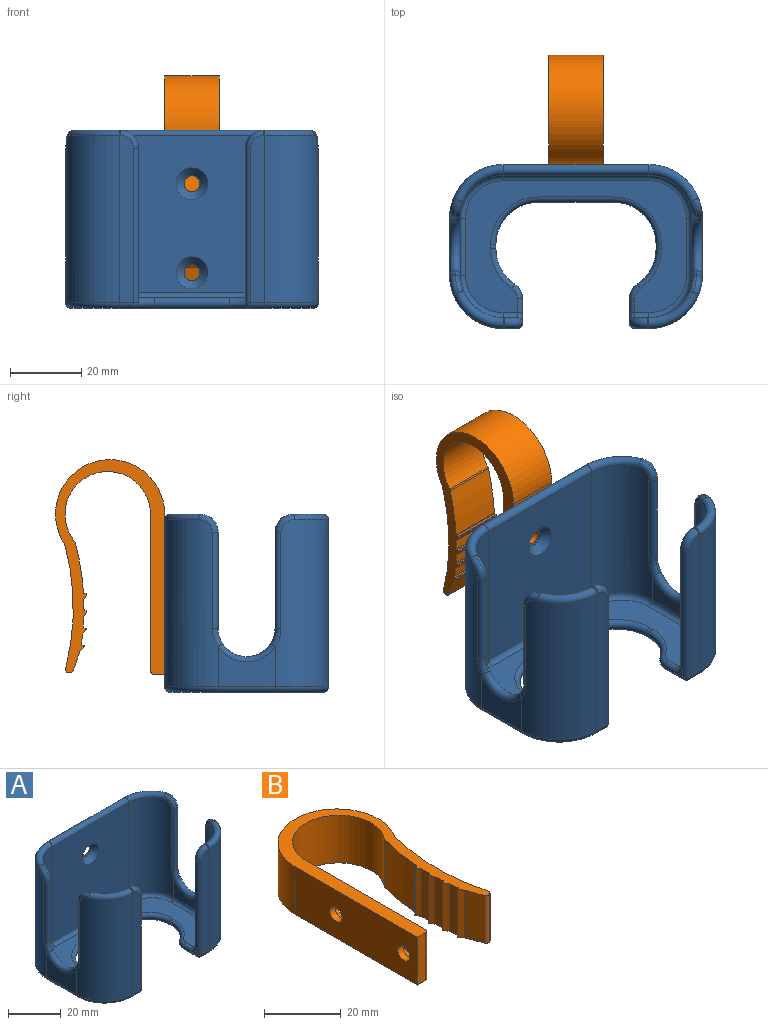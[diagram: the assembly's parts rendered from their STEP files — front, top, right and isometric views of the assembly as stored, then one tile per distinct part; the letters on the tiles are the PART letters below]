
ASSEMBLY  parts=2 mates=1
PART A: 92 faces, bbox 73.5x48.5x50.4 mm
  f0: plane 47x4mm, normal (0,-1,0), area 185.4mm2, adj f16,f69,f73,f77,f78
  f1: plane 62x37mm, normal (0,0,1), area 856.6mm2, adj f48,f52,f53,f57,f59,f62,f63,f67
  f2: plane 44x4mm, normal (0,1,0), area 173.4mm2, adj f12,f69,f73,f77,f80
  f3: plane 16x11.38mm, normal (1,0,0), area 132.7mm2, adj f16,f17,f44,f70
  f4: plane 68x43mm, normal (0,0,-1), area 1325.8mm2, adj f45,f46,f50,f56,f57,f61,f62,f66
  f5: plane 47x4mm, normal (0,-1,0), area 185.4mm2, adj f19,f40,f42,f46,f47
  f6: plane 47x41mm, normal (0,1,0), area 1895.2mm2, adj f17,f18,f30,f61,f88,f90
  f7: plane 16x8.38mm, normal (-1,0,0), area 84.7mm2, adj f12,f15,f44,f72
  f8: plane 44x4mm, normal (0,1,0), area 173.4mm2, adj f13,f40,f42,f47,f52
  f9: plane 16x8.38mm, normal (1,0,0), area 84.7mm2, adj f13,f14,f25,f53
  f10: plane 44x41mm, normal (0,-1,0), area 1677.9mm2, adj f14,f15,f30,f63,f89,f91
  f11: plane 16x11.38mm, normal (-1,0,0), area 132.7mm2, adj f18,f19,f25,f50
  f12: cylinder r=12mm len=44mm, axis (0,0,-1), area 781.6mm2, adj f2,f7,f54,f55,f64,f65,f76
  f13: cylinder r=12mm len=44mm, axis (0,0,1), area 781.6mm2, adj f8,f9,f31,f32,f36,f37,f48
  f14: cylinder r=12mm len=44mm, axis (0,0,-1), area 781.6mm2, adj f9,f10,f22,f26,f27,f28,f59
  f15: cylinder r=12mm len=44mm, axis (0,0,1), area 781.6mm2, adj f7,f10,f33,f38,f39,f43,f68
  f16: cylinder r=15mm len=47mm, axis (0,0,1), area 1047.7mm2, adj f0,f3,f49,f55,f60,f65,f74
  f17: cylinder r=15mm len=47mm, axis (0,0,-1), area 1047.7mm2, adj f3,f6,f33,f35,f39,f41,f66
  f18: cylinder r=15mm len=47mm, axis (0,0,1), area 1047.7mm2, adj f6,f11,f22,f23,f24,f28,f56
  f19: cylinder r=15mm len=47mm, axis (0,0,-1), area 1047.7mm2, adj f5,f11,f29,f31,f34,f36,f45
  f20: plane 3x3mm, normal (1,0,0), area 1.9mm2, adj f47,f57,f58
  f21: plane 3x3mm, normal (-1,0,0), area 1.9mm2, adj f77,f83,f84
  f22: cylinder r=1.5mm len=27mm, axis (0,0,1), area 127.2mm2, adj f14,f18,f23,f24,f26,f27
  f23: bspline ~7x3.44mm, area 12.1mm2, adj f18,f22,f25,f26
  f24: bspline ~6.77x5.33mm, area 18.5mm2, adj f18,f22,f27,f28
  f25: torus R=9.5mm, axis (-1,0,0), area 80.6mm2, adj f9,f11,f23,f26,f29,f32
  f26: bspline ~7x3.08mm, area 10.9mm2, adj f14,f22,f23,f25
  f27: bspline ~6.21x5.34mm, area 15mm2, adj f14,f22,f24,f28
  f28: torus R=13.5mm, axis (0,0,1), area 75.8mm2, adj f14,f18,f24,f27,f30
  f29: bspline ~6x3.18mm, area 12.1mm2, adj f19,f25,f31,f32
  f30: cylinder r=1.5mm len=41mm, axis (1,0,0), area 193.2mm2, adj f6,f10,f28,f33
  f31: cylinder r=1.5mm len=27mm, axis (0,0,-1), area 127.2mm2, adj f13,f19,f29,f32,f34,f37
  f32: bspline ~7.15x3.65mm, area 10.9mm2, adj f13,f25,f29,f31
  f33: torus R=13.5mm, axis (0,0,1), area 75.8mm2, adj f15,f17,f30,f35,f38
  f34: bspline ~6.77x6.19mm, area 18.5mm2, adj f19,f31,f36,f37
  f35: bspline ~6.77x6.19mm, area 18.5mm2, adj f17,f33,f38,f39
  f36: torus R=13.5mm, axis (0,0,1), area 75.8mm2, adj f13,f19,f34,f37,f40
  f37: bspline ~6.21x6.16mm, area 15mm2, adj f13,f31,f34,f36
  f38: bspline ~6.21x6.16mm, area 15mm2, adj f15,f33,f35,f39
  f39: cylinder r=1.5mm len=27mm, axis (0,0,-1), area 127.2mm2, adj f15,f17,f35,f38,f41,f43
  f40: cylinder r=1.5mm len=3mm, axis (-1,0,0), area 2.4mm2, adj f5,f8,f36,f42
  f41: bspline ~7x3.44mm, area 12.1mm2, adj f17,f39,f43,f44
  f42: torus R=3.5mm, axis (0,-1,0), area 33mm2, adj f5,f8,f40,f47
  f43: bspline ~7x3.08mm, area 10.9mm2, adj f15,f39,f41,f44
  f44: torus R=9.5mm, axis (-1,0,0), area 80.6mm2, adj f3,f7,f41,f43,f49,f54
  f45: torus R=13.5mm, axis (0,0,1), area 53.5mm2, adj f4,f19,f46,f50
  f46: cylinder r=1.5mm len=4mm, axis (1,0,0), area 9.4mm2, adj f4,f5,f45,f51
  f47: cylinder r=1.5mm len=43.5mm, axis (0,0,1), area 197.9mm2, adj f5,f8,f20,f42,f51,f58
  f48: torus R=10.5mm, axis (0,0,1), area 42.4mm2, adj f1,f13,f52,f53
  f49: bspline ~7.15x4.05mm, area 12.1mm2, adj f16,f44,f54,f55
  f50: cylinder r=1.5mm len=16mm, axis (0,-1,0), area 37.7mm2, adj f4,f11,f45,f56
  f51: sphere r=1.5mm, area 3.5mm2, adj f46,f47,f57
  f52: cylinder r=1.5mm len=4mm, axis (-1,0,0), area 9.4mm2, adj f1,f8,f48,f58
  f53: cylinder r=1.5mm len=16mm, axis (0,1,0), area 37.7mm2, adj f1,f9,f48,f59
  f54: bspline ~6x2.83mm, area 10.9mm2, adj f12,f44,f49,f55
  f55: cylinder r=1.5mm len=27mm, axis (0,0,1), area 127.2mm2, adj f12,f16,f49,f54,f60,f64
  f56: torus R=13.5mm, axis (0,0,1), area 53.5mm2, adj f4,f18,f50,f61
  f57: cylinder r=1.5mm len=6.9mm, axis (0,-1,0), area 25.5mm2, adj f1,f4,f20,f51,f58,f62
  f58: torus R=3mm, axis (-1,0,0), area 7.6mm2, adj f20,f47,f52,f57
  f59: torus R=10.5mm, axis (0,0,1), area 42.4mm2, adj f1,f14,f53,f63
  f60: bspline ~6.77x5.33mm, area 18.5mm2, adj f16,f55,f64,f65
  f61: cylinder r=1.5mm len=41mm, axis (-1,0,0), area 96.6mm2, adj f4,f6,f56,f66
  f62: torus R=3.5mm, axis (0,0,1), area 20.5mm2, adj f1,f4,f57,f67
  f63: cylinder r=1.5mm len=41mm, axis (1,0,0), area 96.6mm2, adj f1,f10,f59,f68
  f64: bspline ~6.21x5.34mm, area 15mm2, adj f12,f55,f60,f65
  f65: torus R=13.5mm, axis (0,0,1), area 75.8mm2, adj f12,f16,f60,f64,f69
  f66: torus R=13.5mm, axis (0,0,1), area 53.5mm2, adj f4,f17,f61,f70
  f67: torus R=13.5mm, axis (0,0,1), area 57.8mm2, adj f1,f4,f62,f71
  f68: torus R=10.5mm, axis (0,0,1), area 42.4mm2, adj f1,f15,f63,f72
  f69: cylinder r=1.5mm len=3mm, axis (-1,0,0), area 2.4mm2, adj f0,f2,f65,f73
  f70: cylinder r=1.5mm len=16mm, axis (0,1,0), area 37.7mm2, adj f3,f4,f66,f74
  f71: cylinder r=1.5mm len=3mm, axis (0,1,0), area 4.7mm2, adj f1,f4,f67,f75
  f72: cylinder r=1.5mm len=16mm, axis (0,-1,0), area 37.7mm2, adj f1,f7,f68,f76
  f73: torus R=3.5mm, axis (0,-1,0), area 33mm2, adj f0,f2,f69,f77
  f74: torus R=13.5mm, axis (0,0,1), area 53.5mm2, adj f4,f16,f70,f78
  f75: torus R=13.5mm, axis (0,0,1), area 92.9mm2, adj f1,f4,f71,f79
  f76: torus R=10.5mm, axis (0,0,1), area 42.4mm2, adj f1,f12,f72,f80
  f77: cylinder r=1.5mm len=43.5mm, axis (0,0,-1), area 197.9mm2, adj f0,f2,f21,f73,f81,f83
  f78: cylinder r=1.5mm len=4mm, axis (1,0,0), area 9.4mm2, adj f0,f4,f74,f81
  f79: cylinder r=1.5mm len=21mm, axis (1,0,0), area 99mm2, adj f1,f4,f75,f82
  f80: cylinder r=1.5mm len=4mm, axis (-1,0,0), area 9.4mm2, adj f1,f2,f76,f83
  f81: sphere r=1.5mm, area 3.5mm2, adj f77,f78,f84
  f82: torus R=13.5mm, axis (0,0,1), area 92.9mm2, adj f1,f4,f79,f85
  f83: torus R=3mm, axis (-1,0,0), area 7.6mm2, adj f21,f77,f80,f84
  f84: cylinder r=1.5mm len=6.9mm, axis (0,1,0), area 25.5mm2, adj f1,f4,f21,f81,f83,f86
  f85: cylinder r=1.5mm len=3mm, axis (0,-1,0), area 4.7mm2, adj f1,f4,f82,f87
  f86: torus R=3.5mm, axis (0,0,1), area 20.5mm2, adj f1,f4,f84,f87
  f87: torus R=13.5mm, axis (0,0,1), area 57.8mm2, adj f1,f4,f85,f86
  f88: cylinder r=2.25mm len=4.5mm, axis (0,-1,0), area 10.9mm2, adj f6,f89
  f89: cone r=2.25mm half-angle=45deg, axis (0,-1,0), area 66.7mm2, adj f10,f88
  f90: cylinder r=2.25mm len=4.5mm, axis (0,-1,0), area 10.9mm2, adj f6,f91
  f91: cone r=2.25mm half-angle=45deg, axis (0,-1,0), area 66.7mm2, adj f10,f90
PART B: 50 faces, bbox 30.7x60.3x15.2 mm
  f0: cylinder r=2.25mm len=4.5mm, axis (1,0,0), area 28.3mm2, adj f20,f49
  f1: cylinder r=2.25mm len=4.5mm, axis (1,0,0), area 28.3mm2, adj f20,f42
  f2: plane 15.2x3mm, normal (0,-1,0), area 45.6mm2, adj f20,f21,f22,f23
  f3: plane 44x15.2mm, normal (1,0,0), area 583.9mm2, adj f4,f21,f22,f23,f36,f37,f38,f39
  f4: cylinder r=12mm len=24mm, axis (0,0,-1), area 697.2mm2, adj f3,f21,f22,f25
  f5: cylinder r=70mm len=15.2mm, axis (0,0,-1), area 216.7mm2, adj f21,f22,f25,f30
  f6: plane 15.2x0.55mm, normal (0,1,0), area 8.3mm2, adj f21,f22,f30,f32
  f7: plane 15.2x1.43mm, normal (-0.87,-0.5,0), area 25.1mm2, adj f8,f21,f22,f32
  f8: cylinder r=70mm len=15.2mm, axis (0,0,-1), area 44.9mm2, adj f7,f21,f22,f31
  f9: plane 15.2x0.41mm, normal (0,1,0), area 6.3mm2, adj f21,f22,f31,f33
  f10: plane 15.2x1.43mm, normal (-0.87,-0.5,0), area 25.1mm2, adj f11,f21,f22,f33
  f11: cylinder r=70mm len=15.2mm, axis (0,0,-1), area 44.9mm2, adj f10,f21,f22,f28
  f12: plane 15.2x0.43mm, normal (-0.08,1,0), area 6.6mm2, adj f21,f22,f28,f34
  f13: plane 15.2x1.36mm, normal (-0.82,-0.57,0), area 25.1mm2, adj f14,f21,f22,f34
  f14: cylinder r=70mm len=15.2mm, axis (0,0,-1), area 44.9mm2, adj f13,f21,f22,f29
  f15: plane 15.2x0.43mm, normal (-0.15,0.99,0), area 6.6mm2, adj f21,f22,f29,f35
  f16: plane 15.2x1.44mm, normal (-0.78,-0.62,0), area 28.1mm2, adj f21,f22,f26,f35
  f17: plane 15.2x0.21mm, normal (0.27,-0.96,0), area 3.4mm2, adj f21,f22,f24,f27
  f18: cylinder r=67mm len=34.74mm, axis (0,0,-1), area 534.1mm2, adj f19,f21,f22,f24
  f19: cylinder r=15.33mm len=30.66mm, axis (0,0,-1), area 869.3mm2, adj f18,f20,f21,f22
  f20: plane 45x15.2mm, normal (-1,0,0), area 652.2mm2, adj f0,f1,f2,f19,f21,f22
  f21: plane 60.33x30.66mm, normal (0,0,1), area 456.8mm2, adj f2,f3,f4,f5,f6,f7,f8,f9
  f22: plane 60.33x30.66mm, normal (0,0,-1), area 456.8mm2, adj f2,f3,f4,f5,f6,f7,f8,f9
  f23: cylinder r=1mm len=15.2mm, axis (0,0,-1), area 23.9mm2, adj f2,f3,f21,f22
  f24: cylinder r=1mm len=15.2mm, axis (0,0,-1), area 23.7mm2, adj f17,f18,f21,f22
  f25: cylinder r=1mm len=15.2mm, axis (0,0,1), area 6.3mm2, adj f4,f5,f21,f22
  f26: plane 15.2x5.27mm, normal (-0.94,-0.33,0), area 84.9mm2, adj f16,f21,f22,f27
  f27: cylinder r=1mm len=15.2mm, axis (0,0,-1), area 22.8mm2, adj f17,f21,f22,f26
  f28: cylinder r=0.2mm len=15.2mm, axis (0,0,-1), area 4.8mm2, adj f11,f12,f21,f22
  f29: cylinder r=0.2mm len=15.2mm, axis (0,0,-1), area 4.8mm2, adj f14,f15,f21,f22
  f30: cylinder r=0.2mm len=15.2mm, axis (0,0,-1), area 4.6mm2, adj f5,f6,f21,f22
  f31: cylinder r=0.2mm len=15.2mm, axis (0,0,-1), area 4.8mm2, adj f8,f9,f21,f22
  f32: cylinder r=0.2mm len=15.2mm, axis (0,0,-1), area 6.4mm2, adj f6,f7,f21,f22
  f33: cylinder r=0.2mm len=15.2mm, axis (0,0,-1), area 6.4mm2, adj f9,f10,f21,f22
  f34: cylinder r=0.2mm len=15.2mm, axis (0,0,-1), area 6.4mm2, adj f12,f13,f21,f22
  f35: cylinder r=0.2mm len=15.2mm, axis (0,0,-1), area 6.4mm2, adj f15,f16,f21,f22
  f36: plane 3.5x2.02mm, normal (0,-0.5,0.87), area 8.1mm2, adj f3,f37,f41,f42
  f37: plane 4.04x2mm, normal (0,-1,0), area 8.1mm2, adj f3,f36,f38,f42
  f38: plane 3.5x2.02mm, normal (0,-0.5,-0.87), area 8.1mm2, adj f3,f37,f39,f42
  f39: plane 3.5x2.02mm, normal (0,0.5,-0.87), area 8.1mm2, adj f3,f38,f40,f42
  f40: plane 4.04x2mm, normal (0,1,0), area 8.1mm2, adj f3,f39,f41,f42
  f41: plane 3.5x2.02mm, normal (0,0.5,0.87), area 8.1mm2, adj f3,f36,f40,f42
  f42: plane 8.08x7mm, normal (1,0,0), area 26.5mm2, adj f1,f36,f37,f38,f39,f40,f41
  f43: plane 3.5x2.02mm, normal (0,0.5,-0.87), area 8.1mm2, adj f3,f44,f48,f49
  f44: plane 4.04x2mm, normal (0,1,0), area 8.1mm2, adj f3,f43,f45,f49
  f45: plane 3.5x2.02mm, normal (0,0.5,0.87), area 8.1mm2, adj f3,f44,f46,f49
  f46: plane 3.5x2.02mm, normal (0,-0.5,0.87), area 8.1mm2, adj f3,f45,f47,f49
  f47: plane 4.04x2mm, normal (0,-1,0), area 8.1mm2, adj f3,f46,f48,f49
  f48: plane 3.5x2.02mm, normal (0,-0.5,-0.87), area 8.1mm2, adj f3,f43,f47,f49
  f49: plane 8.08x7mm, normal (1,0,0), area 26.5mm2, adj f0,f43,f44,f45,f46,f47,f48
PLACE A t=(-57.72,0.09,-29.42)mm
PLACE B rot(axis=(0.58,0.58,0.58),120deg) t=(-65.32,27.09,-24.42)mm
MATE fastened B.f0 <-> A.f91  axis (0,-1,0) through (-57.72,23.09,5.58)mm
